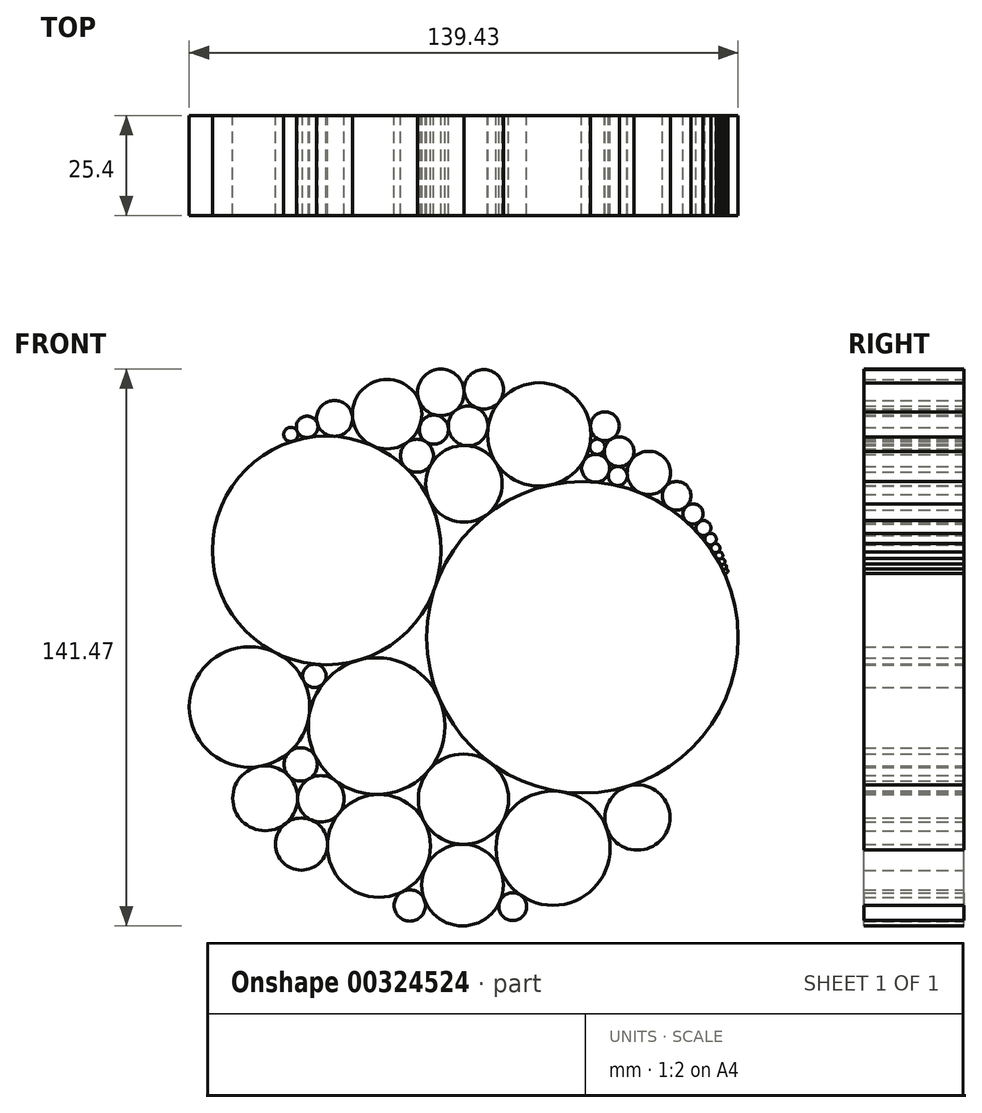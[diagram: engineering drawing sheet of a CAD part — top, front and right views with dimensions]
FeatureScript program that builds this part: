
annotation { "Feature Type Name" : "Feature", "Feature Type Description" : "" }
export const myFeature = defineFeature(function(context is Context, id is Id, definition is map)
    precondition{}
    {
        {
            var Q0;
            Q0=qCreatedBy(makeId("Front.planeOp"),FACE);
            var sketch = newSketch(context, id + "F0", { "sketchPlane" : qUnion([Q0])});
            skCircle(sketch, "E0", {"center": v(0, 0) * mm, "radius": 70.82 * mm});
            skCircle(sketch, "E1", {"center": v(-33.8, 24.57) * mm, "radius": 29.04 * mm});
            skCircle(sketch, "E2", {"center": v(31.16, 2.47) * mm, "radius": 39.56 * mm});
            skCircle(sketch, "E3", {"center": v(-53.4, -15.2) * mm, "radius": 15.3 * mm});
            skCircle(sketch, "E4", {"center": v(-21.11, -20.07) * mm, "radius": 17.36 * mm});
            skCircle(sketch, "E5", {"center": v(20.2, 54.03) * mm, "radius": 13.14 * mm});
            skCircle(sketch, "E6", {"center": v(-36.93, -7.3) * mm, "radius": 2.97 * mm});
            skCircle(sketch, "E7", {"center": v(0.94, -38.63) * mm, "radius": 11.46 * mm});
            skCircle(sketch, "E8", {"center": v(23.72, -51.08) * mm, "radius": 14.5 * mm});
            skCircle(sketch, "E9", {"center": v(-40.4, -29.78) * mm, "radius": 4.24 * mm});
            skCircle(sketch, "E10", {"center": v(1.08, 41.5) * mm, "radius": 9.72 * mm});
            skCircle(sketch, "E11", {"center": v(-10.87, 48.64) * mm, "radius": 4.2 * mm});
            skCircle(sketch, "E12", {"center": v(2.13, 56.24) * mm, "radius": 5.05 * mm});
            skCircle(sketch, "E13", {"center": v(-20.53, -50.5) * mm, "radius": 13.07 * mm});
            skCircle(sketch, "E14", {"center": v(-49.43, -38.4) * mm, "radius": 8.24 * mm});
            skCircle(sketch, "E15", {"center": v(-35.28, -38.54) * mm, "radius": 5.91 * mm});
            skCircle(sketch, "E16", {"center": v(-40.22, -50.05) * mm, "radius": 6.62 * mm});
            skCircle(sketch, "E17", {"center": v(0.69, -60.46) * mm, "radius": 10.37 * mm});
            skCircle(sketch, "E18", {"center": v(45.14, -43.29) * mm, "radius": 8.28 * mm});
            skCircle(sketch, "E19", {"center": v(-6.57, 55.27) * mm, "radius": 3.7 * mm});
            skCircle(sketch, "E20", {"center": v(-38.78, 55.96) * mm, "radius": 2.74 * mm});
            skCircle(sketch, "E21", {"center": v(-31.8, 58.12) * mm, "radius": 4.57 * mm});
            skCircle(sketch, "E22", {"center": v(-42.91, 54.05) * mm, "radius": 1.81 * mm});
            skCircle(sketch, "E23", {"center": v(-18.47, 59.2) * mm, "radius": 8.82 * mm});
            skCircle(sketch, "E24", {"center": v(-4.81, 64.73) * mm, "radius": 5.92 * mm});
            skCircle(sketch, "E25", {"center": v(6.1, 65.5) * mm, "radius": 5.03 * mm});
            skCircle(sketch, "E26", {"center": v(34.52, 45.45) * mm, "radius": 3.55 * mm});
            skCircle(sketch, "E27", {"center": v(34.94, 50.9) * mm, "radius": 1.92 * mm});
            skCircle(sketch, "E28", {"center": v(36.87, 56.15) * mm, "radius": 3.66 * mm});
            skCircle(sketch, "E29", {"center": v(48.03, 44.27) * mm, "radius": 5.5 * mm});
            skCircle(sketch, "E30", {"center": v(40.15, 43.49) * mm, "radius": 2.42 * mm});
            skCircle(sketch, "E31", {"center": v(40.5, 49.67) * mm, "radius": 3.77 * mm});
            skCircle(sketch, "E32", {"center": v(63.97, 61.68) * mm, "radius": 3.94 * mm});
            skCircle(sketch, "E33", {"center": v(56.14, 69.32) * mm, "radius": 2.9 * mm});
            skCircle(sketch, "E34", {"center": v(55.1, 38.45) * mm, "radius": 3.64 * mm});
            skCircle(sketch, "E35", {"center": v(59.27, 33.86) * mm, "radius": 2.57 * mm});
            skCircle(sketch, "E36", {"center": v(61.93, 30.27) * mm, "radius": 1.9 * mm});
            skCircle(sketch, "E37", {"center": v(63.71, 27.44) * mm, "radius": 1.46 * mm});
            skCircle(sketch, "E38", {"center": v(64.97, 25.16) * mm, "radius": 1.15 * mm});
            skCircle(sketch, "E39", {"center": v(65.9, 23.29) * mm, "radius": 0.93 * mm});
            skCircle(sketch, "E40", {"center": v(66.6, 21.74) * mm, "radius": 0.77 * mm});
            skCircle(sketch, "E41", {"center": v(67.14, 20.43) * mm, "radius": 0.65 * mm});
            skCircle(sketch, "E42", {"center": v(67.57, 19.32) * mm, "radius": 0.55 * mm});
            skCircle(sketch, "E43", {"center": v(-12.68, -65.64) * mm, "radius": 3.97 * mm});
            skCircle(sketch, "E44", {"center": v(13.47, -65.93) * mm, "radius": 3.54 * mm});
            skSolve(sketch);
        }
        {
            var Q0;
            {var subQ0=sQuery(id+"F0.wireOp",EDGE,"E2");var subQ8=makeQuery(id+"F0.imprint","INTERSECT",VERTEX,{"derivedFrom":[sQuery(id+"F0.wireOp",EDGE,"E0"),subQ0]});Q0=makeQuery(id+"F0.imprint","IMPRINT",FACE,{"disambiguationData":[TD([[makeQuery(id+"F0.imprint","IMPRINT",EDGE,{"disambiguationData":[TD([[subQ8,-1.0]])],"derivedFrom":subQ0}),1.0]])]});}
            var Q1;
            {var subQ0=sQuery(id+"F0.wireOp",EDGE,"E1");var subQ8=makeQuery(id+"F0.imprint","INTERSECT",VERTEX,{"derivedFrom":[subQ0,sQuery(id+"F0.wireOp",EDGE,"E11")]});Q1=makeQuery(id+"F0.imprint","IMPRINT",FACE,{"disambiguationData":[TD([[makeQuery(id+"F0.imprint","IMPRINT",EDGE,{"disambiguationData":[TD([[subQ8,1.0]])],"derivedFrom":subQ0}),1.0]])]});}
            var Q2;
            {var subQ0=sQuery(id+"F0.wireOp",EDGE,"E10");var subQ5=makeQuery(id+"F0.imprint","INTERSECT",VERTEX,{"derivedFrom":[sQuery(id+"F0.wireOp",EDGE,"E5"),subQ0]});Q2=makeQuery(id+"F0.imprint","IMPRINT",FACE,{"disambiguationData":[TD([[makeQuery(id+"F0.imprint","IMPRINT",EDGE,{"disambiguationData":[TD([[subQ5,-1.0]])],"derivedFrom":subQ0}),1.0]])]});}
            var Q3;
            {var subQ0=sQuery(id+"F0.wireOp",EDGE,"E5");var subQ4=makeQuery(id+"F0.imprint","INTERSECT",VERTEX,{"derivedFrom":[sQuery(id+"F0.wireOp",EDGE,"E0"),subQ0]});Q3=makeQuery(id+"F0.imprint","IMPRINT",FACE,{"disambiguationData":[TD([[makeQuery(id+"F0.imprint","IMPRINT",EDGE,{"disambiguationData":[TD([[subQ4,1.0]])],"derivedFrom":subQ0}),1.0]])]});}
            var Q4;
            {var subQ0=sQuery(id+"F0.wireOp",EDGE,"E12");var subQ4=makeQuery(id+"F0.imprint","INTERSECT",VERTEX,{"derivedFrom":[subQ0,sQuery(id+"F0.wireOp",EDGE,"E24")]});Q4=makeQuery(id+"F0.imprint","IMPRINT",FACE,{"disambiguationData":[TD([[makeQuery(id+"F0.imprint","IMPRINT",EDGE,{"disambiguationData":[TD([[subQ4,1.0]])],"derivedFrom":subQ0}),1.0]])]});}
            var Q5;
            {var subQ0=sQuery(id+"F0.wireOp",EDGE,"E19");var subQ1=makeQuery(id+"F0.imprint","INTERSECT",VERTEX,{"derivedFrom":[sQuery(id+"F0.wireOp",EDGE,"E12"),subQ0]});Q5=makeQuery(id+"F0.imprint","IMPRINT",FACE,{"disambiguationData":[TD([[makeQuery(id+"F0.imprint","IMPRINT",EDGE,{"disambiguationData":[TD([[subQ1,-1.0]])],"derivedFrom":subQ0}),1.0]])]});}
            var Q6;
            {var subQ0=sQuery(id+"F0.wireOp",EDGE,"E11");var subQ1=makeQuery(id+"F0.imprint","INTERSECT",VERTEX,{"derivedFrom":[subQ0,sQuery(id+"F0.wireOp",EDGE,"E23")]});Q6=makeQuery(id+"F0.imprint","IMPRINT",FACE,{"disambiguationData":[TD([[makeQuery(id+"F0.imprint","IMPRINT",EDGE,{"disambiguationData":[TD([[subQ1,1.0]])],"derivedFrom":subQ0}),1.0]])]});}
            var Q7;
            {var subQ0=sQuery(id+"F0.wireOp",EDGE,"E23");var subQ4=makeQuery(id+"F0.imprint","INTERSECT",VERTEX,{"derivedFrom":[sQuery(id+"F0.wireOp",EDGE,"E0"),subQ0]});Q7=makeQuery(id+"F0.imprint","IMPRINT",FACE,{"disambiguationData":[TD([[makeQuery(id+"F0.imprint","IMPRINT",EDGE,{"disambiguationData":[TD([[subQ4,1.0]])],"derivedFrom":subQ0}),1.0]])]});}
            var Q8;
            {var subQ0=sQuery(id+"F0.wireOp",EDGE,"E24");var subQ4=makeQuery(id+"F0.imprint","INTERSECT",VERTEX,{"derivedFrom":[sQuery(id+"F0.wireOp",EDGE,"E0"),subQ0]});Q8=makeQuery(id+"F0.imprint","IMPRINT",FACE,{"disambiguationData":[TD([[makeQuery(id+"F0.imprint","IMPRINT",EDGE,{"disambiguationData":[TD([[subQ4,1.0]])],"derivedFrom":subQ0}),1.0]])]});}
            var Q9;
            {var subQ0=sQuery(id+"F0.wireOp",EDGE,"E25");var subQ1=makeQuery(id+"F0.imprint","INTERSECT",VERTEX,{"derivedFrom":[sQuery(id+"F0.wireOp",EDGE,"E0"),subQ0]});Q9=makeQuery(id+"F0.imprint","IMPRINT",FACE,{"disambiguationData":[TD([[makeQuery(id+"F0.imprint","IMPRINT",EDGE,{"disambiguationData":[TD([[subQ1,-1.0]])],"derivedFrom":subQ0}),1.0]])]});}
            var Q10;
            {var subQ0=sQuery(id+"F0.wireOp",EDGE,"E21");var subQ1=makeQuery(id+"F0.imprint","INTERSECT",VERTEX,{"derivedFrom":[sQuery(id+"F0.wireOp",EDGE,"E0"),subQ0]});Q10=makeQuery(id+"F0.imprint","IMPRINT",FACE,{"disambiguationData":[TD([[makeQuery(id+"F0.imprint","IMPRINT",EDGE,{"disambiguationData":[TD([[subQ1,1.0]])],"derivedFrom":subQ0}),1.0]])]});}
            var Q11;
            {var subQ0=sQuery(id+"F0.wireOp",EDGE,"E22");var subQ1=makeQuery(id+"F0.imprint","INTERSECT",VERTEX,{"derivedFrom":[sQuery(id+"F0.wireOp",EDGE,"E0"),subQ0]});Q11=makeQuery(id+"F0.imprint","IMPRINT",FACE,{"disambiguationData":[TD([[makeQuery(id+"F0.imprint","IMPRINT",EDGE,{"disambiguationData":[TD([[subQ1,1.0]])],"derivedFrom":subQ0}),1.0]])]});}
            var Q12;
            {var subQ0=sQuery(id+"F0.wireOp",EDGE,"E20");var subQ1=makeQuery(id+"F0.imprint","INTERSECT",VERTEX,{"derivedFrom":[sQuery(id+"F0.wireOp",EDGE,"E0"),subQ0]});Q12=makeQuery(id+"F0.imprint","IMPRINT",FACE,{"disambiguationData":[TD([[makeQuery(id+"F0.imprint","IMPRINT",EDGE,{"disambiguationData":[TD([[subQ1,1.0]])],"derivedFrom":subQ0}),1.0]])]});}
            var Q13;
            {var subQ1=sQuery(id+"F0.wireOp",EDGE,"E3");var subQ6=makeQuery(id+"F0.imprint","INTERSECT",VERTEX,{"derivedFrom":[sQuery(id+"F0.wireOp",EDGE,"E1"),subQ1]});Q13=makeQuery(id+"F0.imprint","IMPRINT",FACE,{"disambiguationData":[TD([[makeQuery(id+"F0.imprint","IMPRINT",EDGE,{"disambiguationData":[TD([[subQ6,1.0]])],"derivedFrom":subQ1}),1.0]])]});}
            var Q14;
            {var subQ0=sQuery(id+"F0.wireOp",EDGE,"E4");var subQ4=makeQuery(id+"F0.imprint","INTERSECT",VERTEX,{"derivedFrom":[sQuery(id+"F0.wireOp",EDGE,"E1"),subQ0]});Q14=makeQuery(id+"F0.imprint","IMPRINT",FACE,{"disambiguationData":[TD([[makeQuery(id+"F0.imprint","IMPRINT",EDGE,{"disambiguationData":[TD([[subQ4,1.0]])],"derivedFrom":subQ0}),1.0]])]});}
            var Q15;
            {var subQ0=sQuery(id+"F0.wireOp",EDGE,"E6");var subQ1=makeQuery(id+"F0.imprint","INTERSECT",VERTEX,{"derivedFrom":[sQuery(id+"F0.wireOp",EDGE,"E1"),subQ0]});Q15=makeQuery(id+"F0.imprint","IMPRINT",FACE,{"disambiguationData":[TD([[makeQuery(id+"F0.imprint","IMPRINT",EDGE,{"disambiguationData":[TD([[subQ1,-1.0]])],"derivedFrom":subQ0}),1.0]])]});}
            var Q16;
            {var subQ0=sQuery(id+"F0.wireOp",EDGE,"E9");var subQ1=makeQuery(id+"F0.imprint","INTERSECT",VERTEX,{"derivedFrom":[sQuery(id+"F0.wireOp",EDGE,"E3"),subQ0]});Q16=makeQuery(id+"F0.imprint","IMPRINT",FACE,{"disambiguationData":[TD([[makeQuery(id+"F0.imprint","IMPRINT",EDGE,{"disambiguationData":[TD([[subQ1,1.0]])],"derivedFrom":subQ0}),1.0]])]});}
            var Q17;
            {var subQ0=sQuery(id+"F0.wireOp",EDGE,"E15");var subQ5=makeQuery(id+"F0.imprint","INTERSECT",VERTEX,{"derivedFrom":[sQuery(id+"F0.wireOp",EDGE,"E4"),subQ0]});Q17=makeQuery(id+"F0.imprint","IMPRINT",FACE,{"disambiguationData":[TD([[makeQuery(id+"F0.imprint","IMPRINT",EDGE,{"disambiguationData":[TD([[subQ5,-1.0]])],"derivedFrom":subQ0}),1.0]])]});}
            var Q18;
            {var subQ0=sQuery(id+"F0.wireOp",EDGE,"E13");var subQ4=makeQuery(id+"F0.imprint","INTERSECT",VERTEX,{"derivedFrom":[sQuery(id+"F0.wireOp",EDGE,"E4"),subQ0]});Q18=makeQuery(id+"F0.imprint","IMPRINT",FACE,{"disambiguationData":[TD([[makeQuery(id+"F0.imprint","IMPRINT",EDGE,{"disambiguationData":[TD([[subQ4,1.0]])],"derivedFrom":subQ0}),1.0]])]});}
            var Q19;
            {var subQ0=sQuery(id+"F0.wireOp",EDGE,"E16");var subQ1=makeQuery(id+"F0.imprint","INTERSECT",VERTEX,{"derivedFrom":[sQuery(id+"F0.wireOp",EDGE,"E14"),subQ0]});Q19=makeQuery(id+"F0.imprint","IMPRINT",FACE,{"disambiguationData":[TD([[makeQuery(id+"F0.imprint","IMPRINT",EDGE,{"disambiguationData":[TD([[subQ1,1.0]])],"derivedFrom":subQ0}),1.0]])]});}
            var Q20;
            {var subQ0=sQuery(id+"F0.wireOp",EDGE,"E7");var subQ5=makeQuery(id+"F0.imprint","INTERSECT",VERTEX,{"derivedFrom":[sQuery(id+"F0.wireOp",EDGE,"E2"),subQ0]});Q20=makeQuery(id+"F0.imprint","IMPRINT",FACE,{"disambiguationData":[TD([[makeQuery(id+"F0.imprint","IMPRINT",EDGE,{"disambiguationData":[TD([[subQ5,-1.0]])],"derivedFrom":subQ0}),1.0]])]});}
            var Q21;
            {var subQ0=sQuery(id+"F0.wireOp",EDGE,"E17");var subQ4=makeQuery(id+"F0.imprint","INTERSECT",VERTEX,{"derivedFrom":[sQuery(id+"F0.wireOp",EDGE,"E7"),subQ0]});Q21=makeQuery(id+"F0.imprint","IMPRINT",FACE,{"disambiguationData":[TD([[makeQuery(id+"F0.imprint","IMPRINT",EDGE,{"disambiguationData":[TD([[subQ4,1.0]])],"derivedFrom":subQ0}),1.0]])]});}
            var Q22;
            {var subQ0=sQuery(id+"F0.wireOp",EDGE,"E43");var subQ1=makeQuery(id+"F0.imprint","INTERSECT",VERTEX,{"derivedFrom":[sQuery(id+"F0.wireOp",EDGE,"E13"),subQ0]});Q22=makeQuery(id+"F0.imprint","IMPRINT",FACE,{"disambiguationData":[TD([[makeQuery(id+"F0.imprint","IMPRINT",EDGE,{"disambiguationData":[TD([[subQ1,1.0]])],"derivedFrom":subQ0}),1.0]])]});}
            var Q23;
            {var subQ0=sQuery(id+"F0.wireOp",EDGE,"E44");var subQ1=makeQuery(id+"F0.imprint","INTERSECT",VERTEX,{"derivedFrom":[sQuery(id+"F0.wireOp",EDGE,"E8"),subQ0]});Q23=makeQuery(id+"F0.imprint","IMPRINT",FACE,{"disambiguationData":[TD([[makeQuery(id+"F0.imprint","IMPRINT",EDGE,{"disambiguationData":[TD([[subQ1,-1.0]])],"derivedFrom":subQ0}),1.0]])]});}
            var Q24;
            {var subQ0=sQuery(id+"F0.wireOp",EDGE,"E8");var subQ4=makeQuery(id+"F0.imprint","INTERSECT",VERTEX,{"derivedFrom":[sQuery(id+"F0.wireOp",EDGE,"E2"),subQ0]});Q24=makeQuery(id+"F0.imprint","IMPRINT",FACE,{"disambiguationData":[TD([[makeQuery(id+"F0.imprint","IMPRINT",EDGE,{"disambiguationData":[TD([[subQ4,1.0]])],"derivedFrom":subQ0}),1.0]])]});}
            var Q25;
            {var subQ0=sQuery(id+"F0.wireOp",EDGE,"E18");var subQ1=makeQuery(id+"F0.imprint","INTERSECT",VERTEX,{"derivedFrom":[sQuery(id+"F0.wireOp",EDGE,"E2"),subQ0]});Q25=makeQuery(id+"F0.imprint","IMPRINT",FACE,{"disambiguationData":[TD([[makeQuery(id+"F0.imprint","IMPRINT",EDGE,{"disambiguationData":[TD([[subQ1,-1.0]])],"derivedFrom":subQ0}),1.0]])]});}
            var Q26;
            {var subQ0=sQuery(id+"F0.wireOp",EDGE,"E26");var subQ4=makeQuery(id+"F0.imprint","INTERSECT",VERTEX,{"derivedFrom":[subQ0,sQuery(id+"F0.wireOp",EDGE,"E27")]});Q26=makeQuery(id+"F0.imprint","IMPRINT",FACE,{"disambiguationData":[TD([[makeQuery(id+"F0.imprint","IMPRINT",EDGE,{"disambiguationData":[TD([[subQ4,1.0]])],"derivedFrom":subQ0}),1.0]])]});}
            var Q27;
            {var subQ0=sQuery(id+"F0.wireOp",EDGE,"E31");var subQ4=makeQuery(id+"F0.imprint","INTERSECT",VERTEX,{"derivedFrom":[sQuery(id+"F0.wireOp",EDGE,"E27"),subQ0]});Q27=makeQuery(id+"F0.imprint","IMPRINT",FACE,{"disambiguationData":[TD([[makeQuery(id+"F0.imprint","IMPRINT",EDGE,{"disambiguationData":[TD([[subQ4,1.0]])],"derivedFrom":subQ0}),1.0]])]});}
            var Q28;
            {var subQ0=sQuery(id+"F0.wireOp",EDGE,"E27");var subQ1=makeQuery(id+"F0.imprint","INTERSECT",VERTEX,{"derivedFrom":[sQuery(id+"F0.wireOp",EDGE,"E5"),subQ0]});Q28=makeQuery(id+"F0.imprint","IMPRINT",FACE,{"disambiguationData":[TD([[makeQuery(id+"F0.imprint","IMPRINT",EDGE,{"disambiguationData":[TD([[subQ1,1.0]])],"derivedFrom":subQ0}),1.0]])]});}
            var Q29;
            {var subQ0=sQuery(id+"F0.wireOp",EDGE,"E28");var subQ1=makeQuery(id+"F0.imprint","INTERSECT",VERTEX,{"derivedFrom":[sQuery(id+"F0.wireOp",EDGE,"E0"),subQ0]});Q29=makeQuery(id+"F0.imprint","IMPRINT",FACE,{"disambiguationData":[TD([[makeQuery(id+"F0.imprint","IMPRINT",EDGE,{"disambiguationData":[TD([[subQ1,-1.0]])],"derivedFrom":subQ0}),1.0]])]});}
            var Q30;
            {var subQ0=sQuery(id+"F0.wireOp",EDGE,"E30");var subQ1=makeQuery(id+"F0.imprint","INTERSECT",VERTEX,{"derivedFrom":[sQuery(id+"F0.wireOp",EDGE,"E29"),subQ0]});Q30=makeQuery(id+"F0.imprint","IMPRINT",FACE,{"disambiguationData":[TD([[makeQuery(id+"F0.imprint","IMPRINT",EDGE,{"disambiguationData":[TD([[subQ1,-1.0]])],"derivedFrom":subQ0}),1.0]])]});}
            var Q31;
            {var subQ0=sQuery(id+"F0.wireOp",EDGE,"E29");var subQ5=makeQuery(id+"F0.imprint","INTERSECT",VERTEX,{"derivedFrom":[sQuery(id+"F0.wireOp",EDGE,"E0"),subQ0]});Q31=makeQuery(id+"F0.imprint","IMPRINT",FACE,{"disambiguationData":[TD([[makeQuery(id+"F0.imprint","IMPRINT",EDGE,{"disambiguationData":[TD([[subQ5,-1.0]])],"derivedFrom":subQ0}),1.0]])]});}
            var Q32;
            {var subQ0=sQuery(id+"F0.wireOp",EDGE,"E34");var subQ1=makeQuery(id+"F0.imprint","INTERSECT",VERTEX,{"derivedFrom":[sQuery(id+"F0.wireOp",EDGE,"E0"),subQ0]});Q32=makeQuery(id+"F0.imprint","IMPRINT",FACE,{"disambiguationData":[TD([[makeQuery(id+"F0.imprint","IMPRINT",EDGE,{"disambiguationData":[TD([[subQ1,-1.0]])],"derivedFrom":subQ0}),1.0]])]});}
            var Q33;
            {var subQ0=sQuery(id+"F0.wireOp",EDGE,"E35");var subQ1=makeQuery(id+"F0.imprint","INTERSECT",VERTEX,{"derivedFrom":[sQuery(id+"F0.wireOp",EDGE,"E0"),subQ0]});Q33=makeQuery(id+"F0.imprint","IMPRINT",FACE,{"disambiguationData":[TD([[makeQuery(id+"F0.imprint","IMPRINT",EDGE,{"disambiguationData":[TD([[subQ1,-1.0]])],"derivedFrom":subQ0}),1.0]])]});}
            var Q34;
            {var subQ0=sQuery(id+"F0.wireOp",EDGE,"E36");var subQ1=makeQuery(id+"F0.imprint","INTERSECT",VERTEX,{"derivedFrom":[sQuery(id+"F0.wireOp",EDGE,"E0"),subQ0]});Q34=makeQuery(id+"F0.imprint","IMPRINT",FACE,{"disambiguationData":[TD([[makeQuery(id+"F0.imprint","IMPRINT",EDGE,{"disambiguationData":[TD([[subQ1,-1.0]])],"derivedFrom":subQ0}),1.0]])]});}
            var Q35;
            {var subQ0=sQuery(id+"F0.wireOp",EDGE,"E37");var subQ1=makeQuery(id+"F0.imprint","INTERSECT",VERTEX,{"derivedFrom":[sQuery(id+"F0.wireOp",EDGE,"E0"),subQ0]});Q35=makeQuery(id+"F0.imprint","IMPRINT",FACE,{"disambiguationData":[TD([[makeQuery(id+"F0.imprint","IMPRINT",EDGE,{"disambiguationData":[TD([[subQ1,-1.0]])],"derivedFrom":subQ0}),1.0]])]});}
            var Q36;
            {var subQ0=sQuery(id+"F0.wireOp",EDGE,"E38");var subQ1=makeQuery(id+"F0.imprint","INTERSECT",VERTEX,{"derivedFrom":[sQuery(id+"F0.wireOp",EDGE,"E0"),subQ0]});Q36=makeQuery(id+"F0.imprint","IMPRINT",FACE,{"disambiguationData":[TD([[makeQuery(id+"F0.imprint","IMPRINT",EDGE,{"disambiguationData":[TD([[subQ1,-1.0]])],"derivedFrom":subQ0}),1.0]])]});}
            var Q37;
            {var subQ0=sQuery(id+"F0.wireOp",EDGE,"E39");var subQ1=makeQuery(id+"F0.imprint","INTERSECT",VERTEX,{"derivedFrom":[sQuery(id+"F0.wireOp",EDGE,"E0"),subQ0]});Q37=makeQuery(id+"F0.imprint","IMPRINT",FACE,{"disambiguationData":[TD([[makeQuery(id+"F0.imprint","IMPRINT",EDGE,{"disambiguationData":[TD([[subQ1,-1.0]])],"derivedFrom":subQ0}),1.0]])]});}
            var Q38;
            {var subQ0=sQuery(id+"F0.wireOp",EDGE,"E40");var subQ1=makeQuery(id+"F0.imprint","INTERSECT",VERTEX,{"derivedFrom":[sQuery(id+"F0.wireOp",EDGE,"E0"),subQ0]});Q38=makeQuery(id+"F0.imprint","IMPRINT",FACE,{"disambiguationData":[TD([[makeQuery(id+"F0.imprint","IMPRINT",EDGE,{"disambiguationData":[TD([[subQ1,-1.0]])],"derivedFrom":subQ0}),1.0]])]});}
            var Q39;
            {var subQ0=sQuery(id+"F0.wireOp",EDGE,"E41");var subQ1=makeQuery(id+"F0.imprint","INTERSECT",VERTEX,{"derivedFrom":[sQuery(id+"F0.wireOp",EDGE,"E0"),subQ0]});Q39=makeQuery(id+"F0.imprint","IMPRINT",FACE,{"disambiguationData":[TD([[makeQuery(id+"F0.imprint","IMPRINT",EDGE,{"disambiguationData":[TD([[subQ1,-1.0]])],"derivedFrom":subQ0}),1.0]])]});}
            var Q40;
            {var subQ0=sQuery(id+"F0.wireOp",EDGE,"E42");var subQ1=makeQuery(id+"F0.imprint","INTERSECT",VERTEX,{"derivedFrom":[sQuery(id+"F0.wireOp",EDGE,"E0"),subQ0]});Q40=makeQuery(id+"F0.imprint","IMPRINT",FACE,{"disambiguationData":[TD([[makeQuery(id+"F0.imprint","IMPRINT",EDGE,{"disambiguationData":[TD([[subQ1,-1.0]])],"derivedFrom":subQ0}),1.0]])]});}
            var Q41;
            {var subQ0=sQuery(id+"F0.wireOp",EDGE,"E14");var subQ4=makeQuery(id+"F0.imprint","INTERSECT",VERTEX,{"derivedFrom":[sQuery(id+"F0.wireOp",EDGE,"E3"),subQ0]});Q41=makeQuery(id+"F0.imprint","IMPRINT",FACE,{"disambiguationData":[TD([[makeQuery(id+"F0.imprint","IMPRINT",EDGE,{"disambiguationData":[TD([[subQ4,1.0]])],"derivedFrom":subQ0}),1.0]])]});}
            extrude(context, id + "F1", {"entities" : qUnion([Q0, Q1, Q2, Q3, Q4, Q5, Q6, Q7, Q8, Q9, Q10, Q11, Q12, Q13, Q14, Q15, Q16, Q17, Q18, Q19, Q20, Q21, Q22, Q23, Q24, Q25, Q26, Q27, Q28, Q29, Q30, Q31, Q32, Q33, Q34, Q35, Q36, Q37, Q38, Q39, Q40, Q41]), "depth" : 25.4 * mm});
        }
    });
